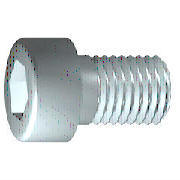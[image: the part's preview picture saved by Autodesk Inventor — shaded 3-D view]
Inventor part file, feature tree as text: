
AUTODESK INVENTOR PART (.ipt)
format: ipt  version: 2022 (Build 260153000, 153)  size: 193,024 bytes
history: native  units: mm (DEFAULTED — no unit token found)
features: sketch x2, other x1, extrude x1, plane x1, fillet x1
ambient origin geometry x7: Origin, YZ Plane, XY Plane, X Axis, Y Axis, Z Axis, Center Point
bodies: Solid1 (feature_tree)
feature tree (6):
  other  "Базовый элемент"
  extrude  "Паз"  Depth=13.9mm
  plane  "Work Plane1"
  fillet  "Fillet2"  Radius=0.429515mm
  sketch  "Эскиз1"
  sketch  "Эскиз2"
